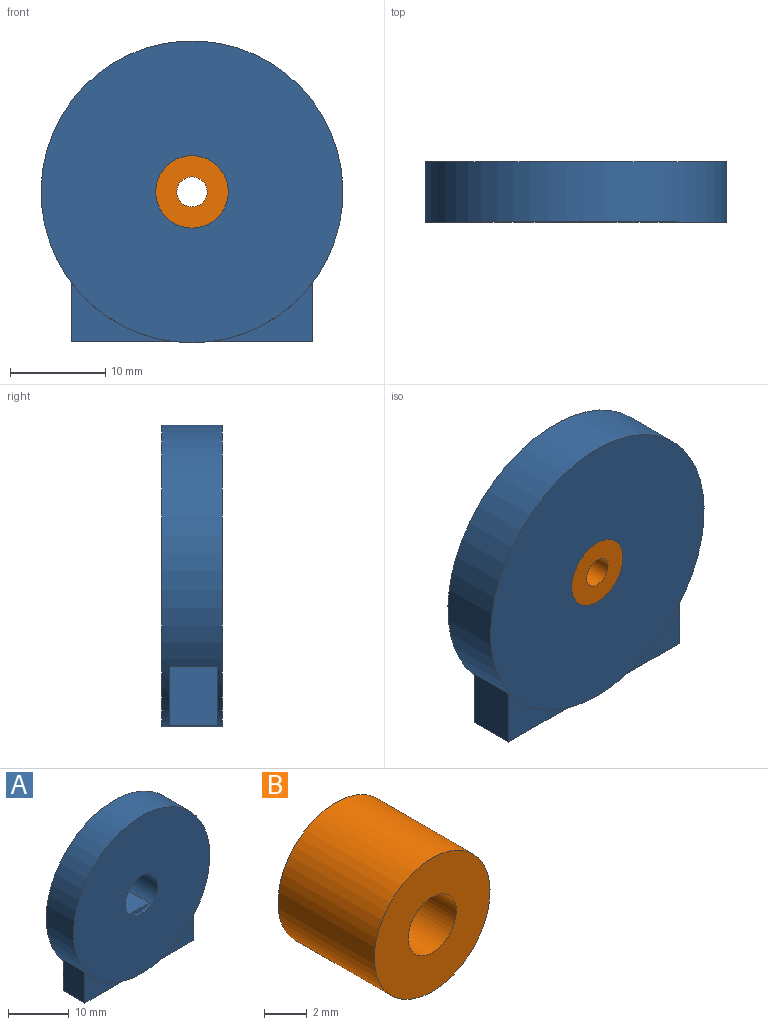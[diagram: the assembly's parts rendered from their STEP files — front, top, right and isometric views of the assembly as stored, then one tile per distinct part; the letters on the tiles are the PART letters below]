
ASSEMBLY  parts=2 mates=1
PART A: 15 faces, bbox 31.8x6.4x31.8 mm
  f0: cylinder r=15.88mm len=31.75mm, axis (0,1,0), area 504.2mm2, adj f2,f3,f4,f5,f6,f7,f8,f9
  f1: cylinder r=3.81mm len=7.62mm, axis (0,1,0), area 127.1mm2, adj f2,f3,f12,f13,f14
  f2: plane 31.75x31.75mm, normal (0,-1,0), area 746.1mm2, adj f0,f1
  f3: plane 31.75x31.75mm, normal (0,1,0), area 746.1mm2, adj f0,f1
  f4: plane 10.7x5.08mm, normal (0,0,-1), area 54.3mm2, adj f0,f5,f6,f7
  f5: plane 10.7x6.22mm, normal (0,-1,0), area 22.8mm2, adj f0,f4,f6
  f6: plane 6.22x5.08mm, normal (-1,0,0), area 31.6mm2, adj f0,f4,f5,f7
  f7: plane 10.7x6.22mm, normal (0,1,0), area 22.8mm2, adj f0,f4,f6
  f8: plane 10.7x5.08mm, normal (0,0,-1), area 54.3mm2, adj f0,f9,f10,f11
  f9: plane 10.7x6.22mm, normal (0,-1,0), area 22.8mm2, adj f0,f8,f11
  f10: plane 10.7x6.22mm, normal (0,1,0), area 22.8mm2, adj f0,f8,f11
  f11: plane 6.22x5.08mm, normal (1,0,0), area 31.6mm2, adj f0,f8,f9,f10
  f12: plane 4.57x0.76mm, normal (0,1,0), area 2.4mm2, adj f1,f14
  f13: plane 4.57x0.76mm, normal (0,-1,0), area 2.4mm2, adj f1,f14
  f14: plane 5.08x4.57mm, normal (0,0,1), area 23.2mm2, adj f1,f12,f13
PART B: 4 faces, bbox 7.6x6.4x7.6 mm
  f0: cylinder r=1.59mm len=6.35mm, axis (0,1,0), area 63.3mm2, adj f2,f3
  f1: cylinder r=3.81mm len=7.62mm, axis (0,1,0), area 152mm2, adj f2,f3
  f2: plane 7.62x7.62mm, normal (0,-1,0), area 37.7mm2, adj f0,f1
  f3: plane 7.62x7.62mm, normal (0,1,0), area 37.7mm2, adj f0,f1
PLACE A t=(-10.06,-1.35,1.93)mm
PLACE B t=(-10.06,-1.35,1.93)mm
MATE fastened B.f1 <-> A.f1  axis (0,1,0) through (-10.06,-1.35,1.93)mm
